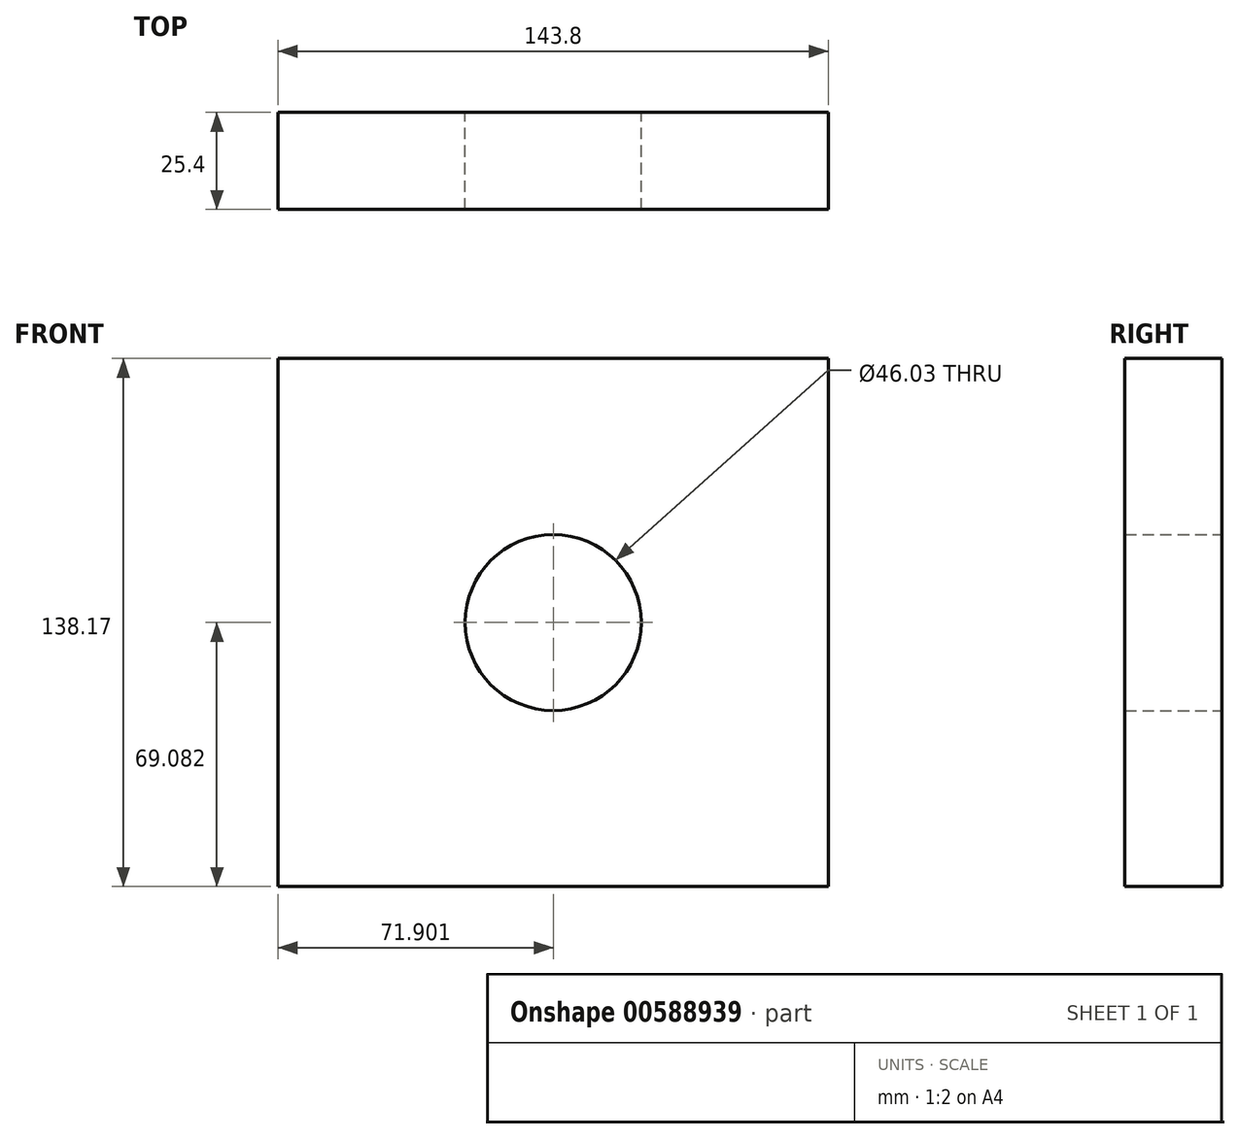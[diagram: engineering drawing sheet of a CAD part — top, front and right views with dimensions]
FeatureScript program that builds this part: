
annotation { "Feature Type Name" : "Feature", "Feature Type Description" : "" }
export const myFeature = defineFeature(function(context is Context, id is Id, definition is map)
    precondition{}
    {
        {
            var Q0;
            Q0=qCreatedBy(makeId("Front.planeOp"),FACE);
            var sketch = newSketch(context, id + "F0", { "sketchPlane" : qUnion([Q0])});
            skLineSegment(sketch, "E0.bottom", {"start": v(45.66, -23.56) * mm, "end": v(-98.14, -23.56) * mm});
            skLineSegment(sketch, "E0.top", {"start": v(45.66, 114.6) * mm, "end": v(-98.14, 114.6) * mm});
            skLineSegment(sketch, "E0.left", {"start": v(45.66, -23.56) * mm, "end": v(45.66, 114.6) * mm});
            skLineSegment(sketch, "E0.right", {"start": v(-98.14, -23.56) * mm, "end": v(-98.14, 114.6) * mm});
            skPoint(sketch, "E0.middle", {"position": v(-26.24, 45.52) * mm});
            skCircle(sketch, "E1", {"center": v(-26.24, 45.52) * mm, "radius": 23.02 * mm});
            skSolve(sketch);
        }
        {
            var Q0;
            Q0 = qSketchRegion(id + "F0", true);
            extrude(context, id + "F1", {"entities" : qUnion([Q0]), "depth" : 25.4 * mm, "offsetDistance" : 25.4 * mm});
        }
    });
